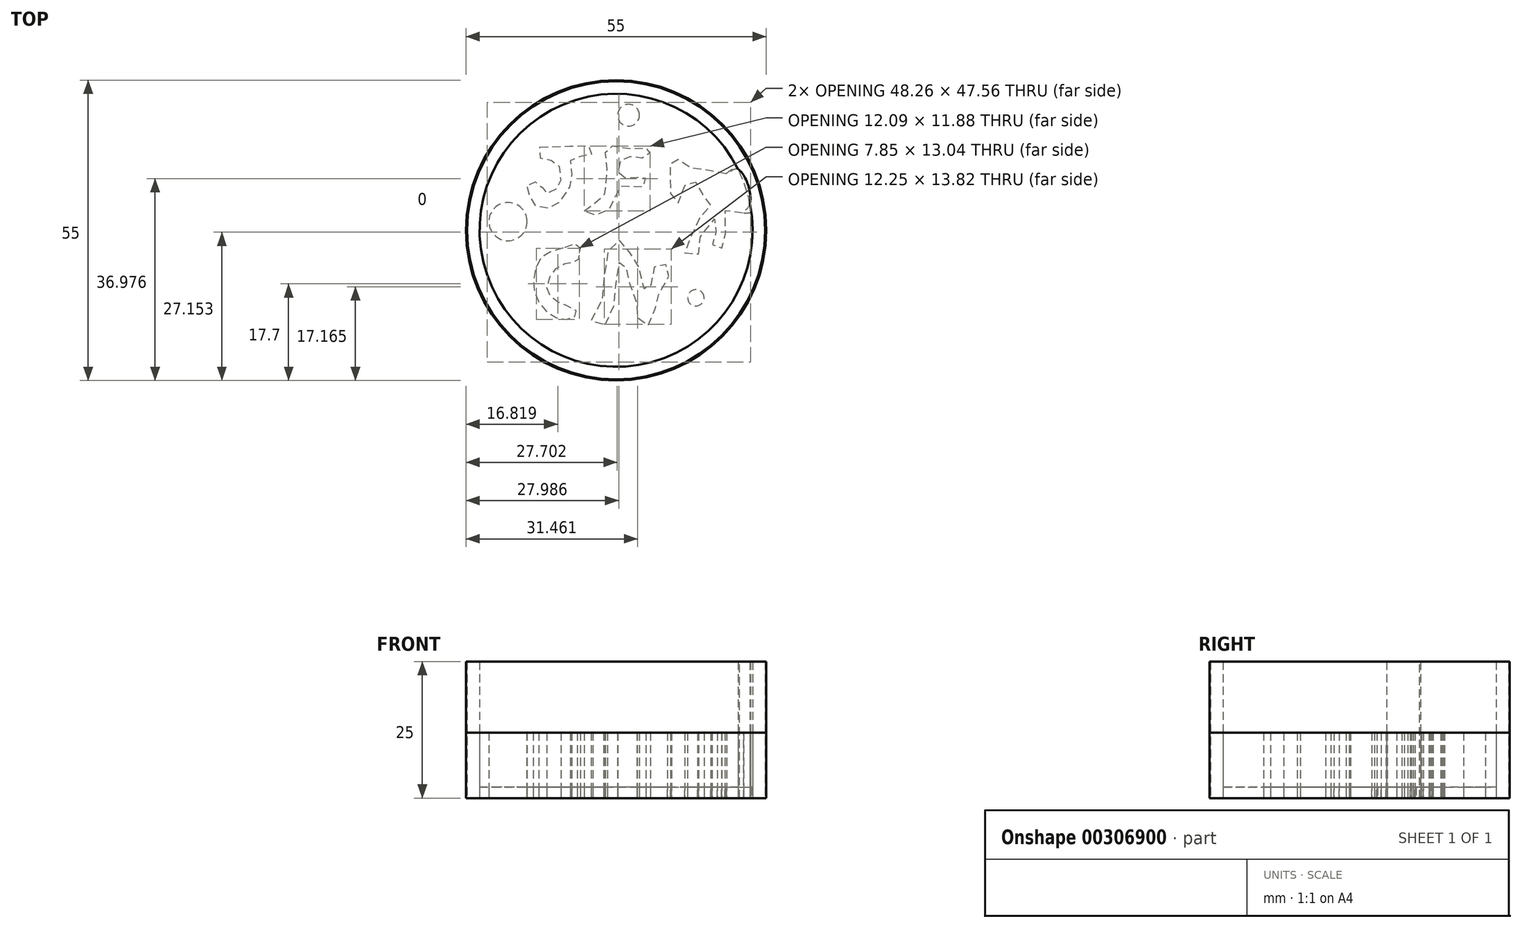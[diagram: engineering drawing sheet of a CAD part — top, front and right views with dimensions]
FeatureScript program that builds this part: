
annotation { "Feature Type Name" : "Feature", "Feature Type Description" : "" }
export const myFeature = defineFeature(function(context is Context, id is Id, definition is map)
    precondition{}
    {
        {
            var Q0;
            Q0=qCreatedBy(makeId("Top.planeOp"),FACE);
            var sketch = newSketch(context, id + "F0", { "sketchPlane" : qUnion([Q0])});
            skCircle(sketch, "E0", {"center": v(0, 0) * mm, "radius": 27.5 * mm});
            skCircle(sketch, "E1", {"center": v(0, 0) * mm, "radius": 25 * mm});
            skFitSpline(sketch, "E2", {"points": [v(-13.96, 15.23) * mm, v(-11.36, 15.23) * mm, v(-4.54, 15.23) * mm, v(-4.87, 13.6) * mm, v(-8.12, 13.28) * mm, v(-8.12, 10.36) * mm, v(-8.77, 7.43) * mm, v(-9.74, 6.14) * mm, v(-11.04, 4.51) * mm, v(-14.29, 4.19) * mm, v(-15.9, 6.46) * mm, v(-16.23, 8.4) * mm, v(-14.29, 8.73) * mm, v(-13.31, 7.43) * mm, v(-12.66, 6.79) * mm, v(-10.71, 7.76) * mm, v(-10.06, 9.7) * mm, v(-11.04, 12.63) * mm, v(-13.64, 12.95) * mm, v(-13.96, 15.23) * mm]});
            skFitSpline(sketch, "E3", {"points": [v(-5.84, 3.54) * mm, v(-2.6, 5.81) * mm, v(-1.95, 7.76) * mm, v(-1.62, 11.33) * mm, v(-1.62, 15.23) * mm, v(3.25, 14.9) * mm, v(6.17, 14.9) * mm, v(5.85, 13.6) * mm, v(3.9, 13.28) * mm, v(1.3, 13.28) * mm, v(0.33, 11) * mm, v(1.3, 9.7) * mm, v(3.9, 9.7) * mm, v(5.2, 9.7) * mm, v(5.2, 8.08) * mm, v(1.95, 8.08) * mm, v(0.98, 8.08) * mm, v(-0.32, 5.81) * mm, v(-2.6, 2.89) * mm, v(-5.84, 3.54) * mm]});
            skFitSpline(sketch, "E4", {"points": [v(-9.74, -3.28) * mm, v(-13.31, -4.58) * mm, v(-14.94, -7.83) * mm, v(-14.94, -11.4) * mm, v(-12.99, -14.65) * mm, v(-10.06, -16.27) * mm, v(-7.8, -15.95) * mm, v(-7.14, -14.97) * mm, v(-9.42, -13.67) * mm, v(-11.36, -12.7) * mm, v(-12.66, -10.75) * mm, v(-11.69, -7.83) * mm, v(-9.74, -6.2) * mm, v(-7.8, -5.88) * mm, v(-6.82, -5.23) * mm, v(-6.82, -2.63) * mm, v(-9.74, -3.28) * mm]});
            skFitSpline(sketch, "E5", {"points": [v(-1.95, -17.24) * mm, v(-0.32, -13.35) * mm, v(0, -9.45) * mm, v(0.98, -5.23) * mm, v(1.95, -7.5) * mm, v(2.6, -10.1) * mm, v(3.9, -14) * mm, v(3.9, -15.95) * mm, v(5.52, -17.57) * mm, v(6.82, -15.62) * mm, v(7.47, -13.02) * mm, v(8.44, -10.43) * mm, v(10.07, -6.85) * mm, v(8.44, -6.2) * mm, v(7.15, -6.53) * mm, v(6.5, -9.45) * mm, v(5.52, -11.4) * mm, v(4.55, -7.83) * mm, v(2.92, -4.58) * mm, v(1.3, -2.63) * mm, v(0, -1.66) * mm, v(-2.27, -7.18) * mm, v(-2.27, -12.05) * mm, v(-4.54, -16.92) * mm, v(-1.95, -17.24) * mm]});
            skFitSpline(sketch, "E6", {"points": [v(10.13, 10.26) * mm, v(10.07, 5.81) * mm, v(11.04, 4.84) * mm, v(12.34, 6.79) * mm, v(13, 9.06) * mm, v(14.29, 9.06) * mm, v(15.59, 7.1) * mm, v(15.91, 6.46) * mm, v(17.21, 5.49) * mm, v(16.89, 3.54) * mm, v(15.26, 2.24) * mm, v(13.64, -1.33) * mm, v(12.67, -3.93) * mm, v(12.67, -4.26) * mm, v(14.94, -4.58) * mm, v(14.94, -2.96) * mm, v(16.24, 0) * mm, v(18.37, 2.24) * mm, v(18.37, 0) * mm, v(18, -1.97) * mm, v(18, -1.97) * mm, v(17.62, -3.2) * mm, v(19.18, -3.61) * mm, v(19.3, -2.03) * mm, v(20.2, 0) * mm, v(20.13, 3.86) * mm, v(23.38, 3.21) * mm, v(24.5, 4.94) * mm, v(22.37, 11.16) * mm, v(20.13, 10.36) * mm, v(17.21, 10.68) * mm, v(15.91, 11.66) * mm, v(12.02, 11.66) * mm, v(11.37, 12.95) * mm, v(10.93, 11.4) * mm, v(9.42, 13.28) * mm, v(10.13, 10.26) * mm]});
            skCircle(sketch, "E7", {"center": v(2.27, 21.07) * mm, "radius": 2 * mm});
            skCircle(sketch, "E8", {"center": v(-19.8, 1.59) * mm, "radius": 3.5 * mm});
            skCircle(sketch, "E9", {"center": v(14.61, -12.37) * mm, "radius": 1.5 * mm});
            skFitSpline(sketch, "E10", {"points": [v(20.13, 10.36) * mm, v(22.37, 11.16) * mm, v(24.5, 4.94) * mm, v(23.38, 3.21) * mm, v(35.64, 5.97) * mm], "startDerivative": vector(12.97, 10.9) * mm, "endDerivative": vector(46.48, 12.26) * mm});
            skSolve(sketch);
        }
        {
            var Q0;
            Q0 = qSketchRegion(id + "F0", true);
            var Q1;
            Q1=makeQuery(id+"F0.imprint","IMPRINT",FACE,{"disambiguationData":[TD([[makeQuery(id+"F0.imprint","IMPRINT",EDGE,{"derivedFrom":sQuery(id+"F0.wireOp",EDGE,"E2")}),-1.0]])]});
            var Q2;
            Q2=makeQuery(id+"F0.imprint","IMPRINT",FACE,{"disambiguationData":[TD([[makeQuery(id+"F0.imprint","IMPRINT",EDGE,{"derivedFrom":sQuery(id+"F0.wireOp",EDGE,"E3")}),-1.0]])]});
            var Q3;
            Q3=makeQuery(id+"F0.imprint","IMPRINT",FACE,{"disambiguationData":[TD([[makeQuery(id+"F0.imprint","IMPRINT",EDGE,{"derivedFrom":sQuery(id+"F0.wireOp",EDGE,"E8")}),1.0]])]});
            var Q4;
            Q4=makeQuery(id+"F0.imprint","IMPRINT",FACE,{"disambiguationData":[TD([[makeQuery(id+"F0.imprint","IMPRINT",EDGE,{"derivedFrom":sQuery(id+"F0.wireOp",EDGE,"E4")}),1.0]])]});
            var Q5;
            Q5=makeQuery(id+"F0.imprint","IMPRINT",FACE,{"disambiguationData":[TD([[makeQuery(id+"F0.imprint","IMPRINT",EDGE,{"derivedFrom":sQuery(id+"F0.wireOp",EDGE,"E5")}),1.0]])]});
            var Q6;
            Q6=makeQuery(id+"F0.imprint","IMPRINT",FACE,{"disambiguationData":[TD([[makeQuery(id+"F0.imprint","IMPRINT",EDGE,{"derivedFrom":sQuery(id+"F0.wireOp",EDGE,"E7")}),1.0]])]});
            var Q7;
            Q7=makeQuery(id+"F0.imprint","IMPRINT",FACE,{"disambiguationData":[TD([[makeQuery(id+"F0.imprint","IMPRINT",EDGE,{"derivedFrom":sQuery(id+"F0.wireOp",EDGE,"E9")}),1.0]])]});
            extrude(context, id + "F1", {"entities" : qUnion([Q0, Q1, Q2, Q3, Q4, Q5, Q6, Q7]), "depth" : 12 * mm});
        }
        {
            var Q0;
            Q0=qCreatedBy(makeId("Top.planeOp"),FACE);
            var sketch = newSketch(context, id + "F2", { "sketchPlane" : qUnion([Q0])});
            skCircle(sketch, "E11", {"center": v(0, 0) * mm, "radius": 27.3 * mm});
            skSolve(sketch);
        }
        {
            var Q0;
            Q0 = qSketchRegion(id + "F0", true);
            extrude(context, id + "F3", {"entities" : qUnion([Q0]), "operationType" : NewBodyOperationType.ADD, "depth" : 12 * mm});
        }
        {
            var Q0;
            Q0=makeQuery(id+"F0.imprint","IMPRINT",FACE,{"disambiguationData":[TD([[makeQuery(id+"F0.imprint","IMPRINT",EDGE,{"derivedFrom":sQuery(id+"F0.wireOp",EDGE,"E6")}),1.0]])]});
            extrude(context, id + "F4", {"entities" : qUnion([Q0]), "operationType" : NewBodyOperationType.ADD, "depth" : 12 * mm});
        }
        {
            var Q0;
            Q0=makeQuery(id+"F0.imprint","IMPRINT",FACE,{"disambiguationData":[TD([[makeQuery(id+"F0.imprint","IMPRINT",EDGE,{"derivedFrom":sQuery(id+"F0.wireOp",EDGE,"E2")}),1.0]])]});
            extrude(context, id + "F5", {"entities" : qUnion([Q0]), "depth" : 2 * mm});
        }
        {
            var Q0;
            Q0 = qSketchRegion(id + "F0", true);
            var Q1;
            Q1 = qSketchRegion(id + "F2", true);
            extrude(context, id + "F6", {"entities" : qUnion([Q0, Q1]), "depth" : 25 * mm});
        }
    });
